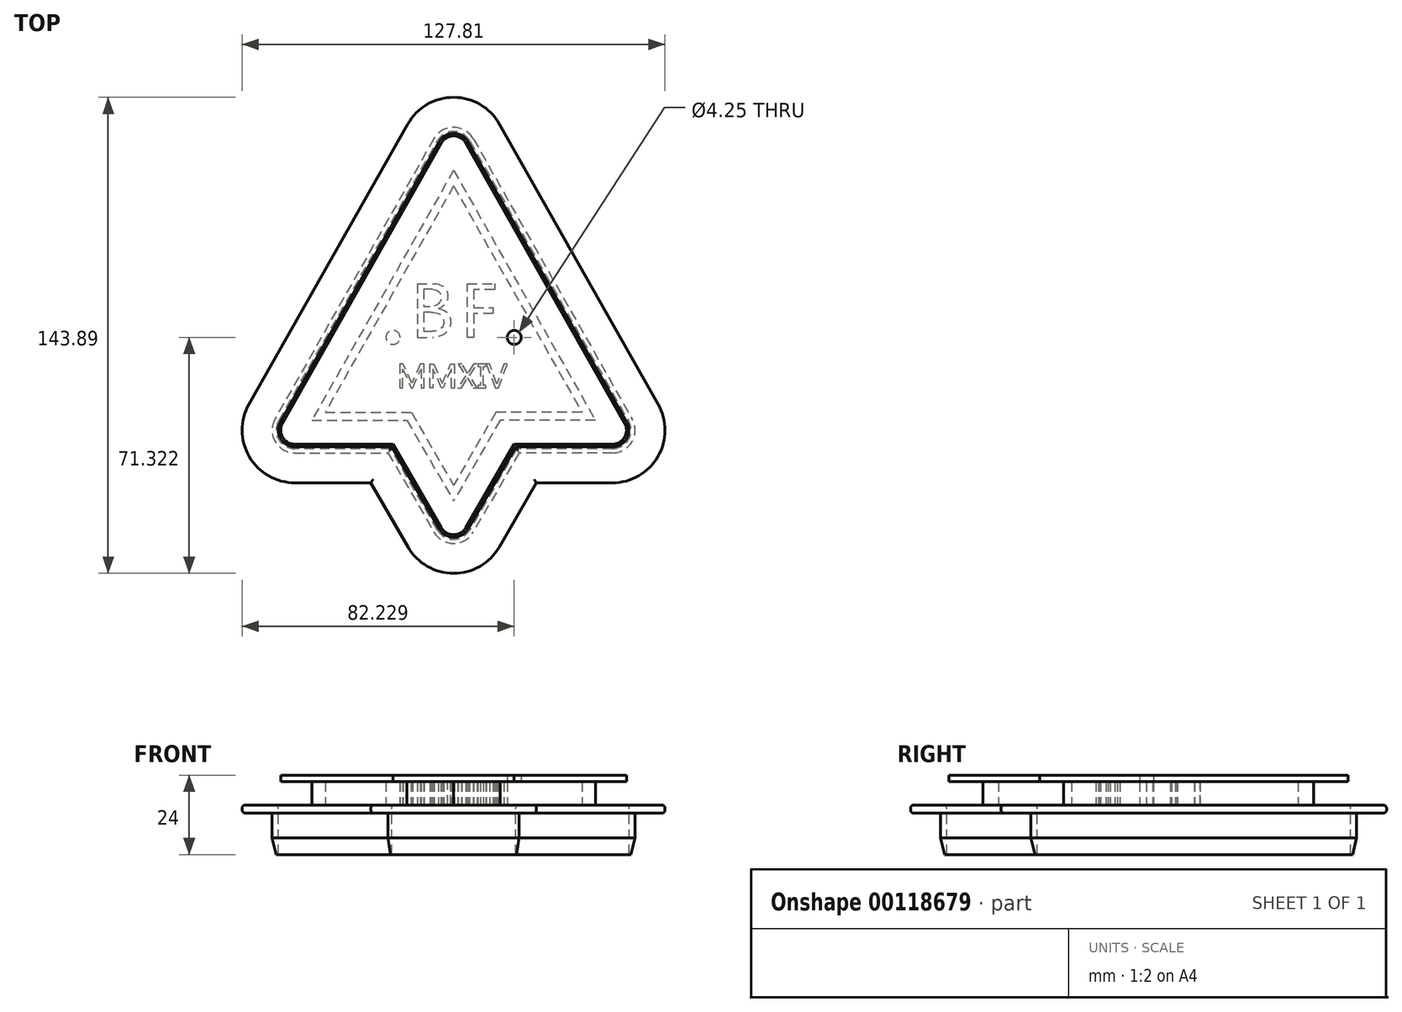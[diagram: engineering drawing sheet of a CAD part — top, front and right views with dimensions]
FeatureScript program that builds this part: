
annotation { "Feature Type Name" : "Feature", "Feature Type Description" : "" }
export const myFeature = defineFeature(function(context is Context, id is Id, definition is map)
    precondition{}
    {
        {
            var Q0;
            Q0=qCreatedBy(makeId("Top.planeOp"),FACE);
            var sketch = newSketch(context, id + "F0", { "sketchPlane" : qUnion([Q0])});
            skLineSegment(sketch, "E0", {"start": v(3.45, -76.83) * mm, "end": v(3.45, 23.17) * mm, "construction": true});
            skLineSegment(sketch, "E1", {"start": v(3.45, 23.17) * mm, "end": v(-39.41, -52.46) * mm});
            skLineSegment(sketch, "E2", {"start": v(-39.41, -52.46) * mm, "end": v(-10.65, -52.46) * mm});
            skLineSegment(sketch, "E3", {"start": v(-10.65, -52.46) * mm, "end": v(3.45, -76.83) * mm});
            skLineSegment(sketch, "E4.MirrorCS", {"start": v(17.54, -52.46) * mm, "end": v(3.45, -76.83) * mm});
            skLineSegment(sketch, "E5.MirrorCS", {"start": v(46.3, -52.46) * mm, "end": v(17.54, -52.46) * mm});
            skLineSegment(sketch, "E6.MirrorCS", {"start": v(3.45, 23.17) * mm, "end": v(46.3, -52.46) * mm});
            skLineSegment(sketch, "E7.0", {"start": v(7.8, 31.72) * mm, "end": v(55.8, -53) * mm});
            skLineSegment(sketch, "E7.1", {"start": v(-44.56, -60.46) * mm, "end": v(-15.26, -60.46) * mm});
            skLineSegment(sketch, "E7.2", {"start": v(-15.26, -60.46) * mm, "end": v(-0.88, -85.33) * mm});
            skLineSegment(sketch, "E7.3", {"start": v(-0.9, 31.72) * mm, "end": v(-48.9, -53) * mm});
            skLineSegment(sketch, "E7.4", {"start": v(22.16, -60.46) * mm, "end": v(7.77, -85.33) * mm});
            skLineSegment(sketch, "E7.5", {"start": v(51.45, -60.46) * mm, "end": v(22.16, -60.46) * mm});
            skLineSegment(sketch, "E8.0", {"start": v(3.45, 18.38) * mm, "end": v(42.25, -50.1) * mm});
            skLineSegment(sketch, "E8.1", {"start": v(-35.36, -50.1) * mm, "end": v(-9.29, -50.1) * mm});
            skLineSegment(sketch, "E8.2", {"start": v(-9.29, -50.1) * mm, "end": v(3.45, -72.12) * mm});
            skLineSegment(sketch, "E8.3", {"start": v(3.45, 18.38) * mm, "end": v(-35.36, -50.1) * mm});
            skLineSegment(sketch, "E8.4", {"start": v(16.18, -50.1) * mm, "end": v(3.45, -72.12) * mm});
            skLineSegment(sketch, "E8.5", {"start": v(42.25, -50.1) * mm, "end": v(16.18, -50.1) * mm});
            skPoint(sketch, "E9.visualSharp", {"position": v(3.45, 39.4) * mm});
            skArc(sketch, "E9.filletArc", {"start": v(7.8, 31.72) * mm, "mid": v(3.45, 34.25) * mm, "end": v(-0.9, 31.72) * mm});
            skPoint(sketch, "E10.visualSharp", {"position": v(-53.14, -60.46) * mm});
            skArc(sketch, "E10.filletArc", {"start": v(-48.9, -53) * mm, "mid": v(-48.88, -57.98) * mm, "end": v(-44.56, -60.46) * mm});
            skPoint(sketch, "E11.visualSharp", {"position": v(3.45, -92.81) * mm});
            skArc(sketch, "E11.filletArc", {"start": v(-0.88, -85.33) * mm, "mid": v(3.45, -87.82) * mm, "end": v(7.77, -85.33) * mm});
            skPoint(sketch, "E12.visualSharp", {"position": v(60.03, -60.46) * mm});
            skArc(sketch, "E12.filletArc", {"start": v(51.45, -60.46) * mm, "mid": v(55.77, -57.98) * mm, "end": v(55.8, -53) * mm});
            skLineSegment(sketch, "E13", {"start": v(-7.57, -11.13) * mm, "end": v(-7.57, -27.4) * mm});
            skLineSegment(sketch, "E14", {"start": v(-7.57, -27.4) * mm, "end": v(-2.15, -27.4) * mm});
            skLineSegment(sketch, "E15", {"start": v(-7.57, -11.13) * mm, "end": v(-2.43, -11.13) * mm});
            skLineSegment(sketch, "E16", {"start": v(-2.95, -12.9) * mm, "end": v(-5.58, -12.9) * mm});
            skLineSegment(sketch, "E17", {"start": v(-5.58, -12.9) * mm, "end": v(-5.58, -18.07) * mm});
            skLineSegment(sketch, "E18", {"start": v(-5.58, -18.07) * mm, "end": v(-3.65, -18.07) * mm});
            skLineSegment(sketch, "E19", {"start": v(-3.3, -19.84) * mm, "end": v(-5.58, -19.84) * mm});
            skLineSegment(sketch, "E20", {"start": v(-5.58, -19.84) * mm, "end": v(-5.58, -25.6) * mm});
            skLineSegment(sketch, "E21", {"start": v(-5.58, -25.6) * mm, "end": v(-2.88, -25.6) * mm});
            skFitSpline(sketch, "E22", {"points": [v(-2.95, -12.9) * mm, v(-1.55, -13.25) * mm, v(-0.77, -13.84) * mm, v(-0.4, -14.71) * mm, v(-0.38, -15.73) * mm, v(-0.61, -16.54) * mm, v(-1.06, -17.17) * mm, v(-1.75, -17.68) * mm, v(-2.43, -17.93) * mm, v(-3.27, -18.06) * mm, v(-3.65, -18.07) * mm], "startDerivative": vector(12.37, 0) * mm, "endDerivative": vector(-6.52, 0) * mm});
            skFitSpline(sketch, "E23", {"points": [v(-3.3, -19.84) * mm, v(-3.1, -19.84) * mm, v(-2.41, -19.88) * mm, v(-1.62, -20.03) * mm, v(-1.02, -20.26) * mm, v(-0.58, -20.52) * mm, v(-0.1, -20.94) * mm, v(0.27, -21.55) * mm, v(0.42, -22.11) * mm, v(0.46, -22.89) * mm, v(0.36, -23.57) * mm, v(0.05, -24.23) * mm, v(-0.37, -24.74) * mm, v(-0.99, -25.18) * mm, v(-1.82, -25.49) * mm, v(-2.55, -25.6) * mm, v(-2.88, -25.6) * mm], "startDerivative": vector(4.87, 0.06) * mm, "endDerivative": vector(-6.62, 0.23) * mm});
            skFitSpline(sketch, "E24", {"points": [v(-2.43, -11.13) * mm, v(-2.2, -11.13) * mm, v(-1.28, -11.3) * mm, v(-0.51, -11.57) * mm, v(0.21, -11.98) * mm, v(0.77, -12.45) * mm, v(1.21, -13.02) * mm, v(1.52, -13.67) * mm, v(1.66, -14.33) * mm, v(1.7, -15.05) * mm, v(1.6, -15.83) * mm, v(1.15, -16.97) * mm, v(0.59, -17.7) * mm, v(-0.29, -18.37) * mm, v(-1.14, -18.73) * mm], "startDerivative": vector(4.9, 0.32) * mm, "endDerivative": vector(-10.98, -3.88) * mm});
            skFitSpline(sketch, "E25", {"points": [v(-1.14, -18.73) * mm, v(-0.6, -18.81) * mm, v(0.06, -19) * mm, v(0.6, -19.25) * mm, v(1.07, -19.56) * mm, v(1.52, -19.96) * mm, v(1.92, -20.5) * mm, v(2.25, -21.13) * mm, v(2.45, -21.89) * mm, v(2.5, -22.84) * mm, v(2.41, -23.7) * mm, v(2.14, -24.56) * mm, v(1.71, -25.3) * mm, v(1.04, -26.04) * mm, v(0.2, -26.65) * mm, v(-0.94, -27.14) * mm, v(-2.04, -27.35) * mm, v(-2.81, -27.4) * mm], "startDerivative": vector(10.65, -1.4) * mm, "endDerivative": vector(-12.84, -0.61) * mm});
            skCircle(sketch, "E26", {"center": v(-14.88, -27.4) * mm, "radius": 2.13 * mm});
            skCircle(sketch, "E27.MirrorC", {"center": v(21.77, -27.4) * mm, "radius": 2.13 * mm});
            skLineSegment(sketch, "E28", {"start": v(7.57, -11.13) * mm, "end": v(15.83, -11.13) * mm});
            skLineSegment(sketch, "E29", {"start": v(15.83, -11.13) * mm, "end": v(15.83, -12.93) * mm});
            skLineSegment(sketch, "E30", {"start": v(15.83, -12.93) * mm, "end": v(9.53, -12.93) * mm});
            skLineSegment(sketch, "E31", {"start": v(9.53, -12.93) * mm, "end": v(9.53, -18.43) * mm});
            skLineSegment(sketch, "E32", {"start": v(9.53, -18.43) * mm, "end": v(15.38, -18.43) * mm});
            skLineSegment(sketch, "E33", {"start": v(15.38, -18.43) * mm, "end": v(15.38, -20.22) * mm});
            skLineSegment(sketch, "E34", {"start": v(15.38, -20.22) * mm, "end": v(9.53, -20.22) * mm});
            skLineSegment(sketch, "E35", {"start": v(9.53, -20.22) * mm, "end": v(9.53, -27.4) * mm});
            skLineSegment(sketch, "E36", {"start": v(9.53, -27.4) * mm, "end": v(7.57, -27.4) * mm});
            skLineSegment(sketch, "E37", {"start": v(7.57, -27.4) * mm, "end": v(7.57, -11.13) * mm});
            skLineSegment(sketch, "E38", {"start": v(-13.1, -42.69) * mm, "end": v(20.07, -42.69) * mm, "construction": true});
            skLineSegment(sketch, "E39", {"start": v(20.07, -42.69) * mm, "end": v(20.07, -35.42) * mm, "construction": true});
            skLineSegment(sketch, "E40", {"start": v(20.07, -35.42) * mm, "end": v(-13.1, -35.42) * mm, "construction": true});
            skLineSegment(sketch, "E41", {"start": v(-12.88, -35.42) * mm, "end": v(-12.88, -42.69) * mm});
            skLineSegment(sketch, "E42", {"start": v(-12.88, -42.69) * mm, "end": v(-11.95, -42.69) * mm});
            skLineSegment(sketch, "E43", {"start": v(-11.95, -42.69) * mm, "end": v(-11.95, -36.93) * mm});
            skLineSegment(sketch, "E44", {"start": v(-11.95, -36.93) * mm, "end": v(-9.4, -42.69) * mm});
            skLineSegment(sketch, "E45", {"start": v(-9.4, -42.69) * mm, "end": v(-8.95, -42.69) * mm});
            skLineSegment(sketch, "E46", {"start": v(-8.95, -42.69) * mm, "end": v(-6.4, -36.93) * mm});
            skLineSegment(sketch, "E47", {"start": v(-6.4, -36.93) * mm, "end": v(-6.4, -42.69) * mm});
            skLineSegment(sketch, "E48", {"start": v(-6.4, -42.69) * mm, "end": v(-5.46, -42.69) * mm});
            skLineSegment(sketch, "E49", {"start": v(-5.46, -42.69) * mm, "end": v(-5.46, -35.42) * mm});
            skLineSegment(sketch, "E50", {"start": v(-5.46, -35.42) * mm, "end": v(-6.6, -35.42) * mm});
            skLineSegment(sketch, "E51", {"start": v(-6.6, -35.42) * mm, "end": v(-9.18, -41.27) * mm});
            skLineSegment(sketch, "E52", {"start": v(-9.18, -41.27) * mm, "end": v(-11.77, -35.42) * mm});
            skLineSegment(sketch, "E53", {"start": v(-11.77, -35.42) * mm, "end": v(-12.88, -35.42) * mm});
            skLineSegment(sketch, "E54", {"start": v(-5.46, -42.69) * mm, "end": v(-3.71, -42.69) * mm});
            skLineSegment(sketch, "E55", {"start": v(-4.59, -42.69) * mm, "end": v(-4.59, -35.42) * mm, "construction": true});
            skLineSegment(sketch, "E56.MirrorCS", {"start": v(-3.71, -42.69) * mm, "end": v(-3.71, -35.42) * mm});
            skLineSegment(sketch, "E57.MirrorCS", {"start": v(-2.78, -36.93) * mm, "end": v(-2.78, -42.69) * mm});
            skLineSegment(sketch, "E58.MirrorCS", {"start": v(-0.23, -42.69) * mm, "end": v(-2.78, -36.93) * mm});
            skLineSegment(sketch, "E59.MirrorCS", {"start": v(-2.59, -35.42) * mm, "end": v(0, -41.27) * mm});
            skLineSegment(sketch, "E60.MirrorCS", {"start": v(-29.24, -35.42) * mm, "end": v(3.91, -35.42) * mm, "construction": true});
            skLineSegment(sketch, "E61.MirrorCS", {"start": v(0, -41.27) * mm, "end": v(2.59, -35.42) * mm});
            skLineSegment(sketch, "E62.MirrorCS", {"start": v(2.77, -36.93) * mm, "end": v(0.23, -42.69) * mm});
            skLineSegment(sketch, "E63.MirrorCS", {"start": v(2.77, -42.69) * mm, "end": v(2.77, -36.93) * mm});
            skLineSegment(sketch, "E64.MirrorCS", {"start": v(3.7, -35.42) * mm, "end": v(3.7, -42.69) * mm});
            skLineSegment(sketch, "E65", {"start": v(-3.71, -35.42) * mm, "end": v(-2.59, -35.42) * mm});
            skLineSegment(sketch, "E66", {"start": v(2.59, -35.42) * mm, "end": v(3.7, -35.42) * mm});
            skLineSegment(sketch, "E67", {"start": v(2.77, -42.69) * mm, "end": v(3.7, -42.69) * mm});
            skLineSegment(sketch, "E68", {"start": v(0.23, -42.69) * mm, "end": v(-0.23, -42.69) * mm});
            skLineSegment(sketch, "E69", {"start": v(-2.78, -42.69) * mm, "end": v(-3.71, -42.69) * mm});
            skLineSegment(sketch, "E70", {"start": v(4.83, -35.42) * mm, "end": v(7.09, -39.05) * mm});
            skLineSegment(sketch, "E71", {"start": v(7.09, -39.05) * mm, "end": v(4.64, -42.69) * mm});
            skLineSegment(sketch, "E72", {"start": v(4.64, -42.69) * mm, "end": v(5.8, -42.69) * mm});
            skLineSegment(sketch, "E73", {"start": v(5.8, -42.69) * mm, "end": v(7.63, -39.64) * mm});
            skLineSegment(sketch, "E74", {"start": v(7.63, -39.64) * mm, "end": v(9.44, -42.69) * mm});
            skLineSegment(sketch, "E75", {"start": v(9.44, -42.69) * mm, "end": v(10.56, -42.69) * mm});
            skLineSegment(sketch, "E76", {"start": v(10.56, -42.69) * mm, "end": v(8.26, -39.05) * mm});
            skLineSegment(sketch, "E77", {"start": v(8.26, -39.05) * mm, "end": v(10.54, -35.42) * mm});
            skLineSegment(sketch, "E78", {"start": v(10.54, -35.42) * mm, "end": v(9.48, -35.42) * mm});
            skLineSegment(sketch, "E79", {"start": v(9.48, -35.42) * mm, "end": v(7.67, -38.4) * mm});
            skLineSegment(sketch, "E80", {"start": v(7.67, -38.4) * mm, "end": v(5.94, -35.42) * mm});
            skLineSegment(sketch, "E81", {"start": v(5.94, -35.42) * mm, "end": v(4.83, -35.42) * mm});
            skLineSegment(sketch, "E82", {"start": v(10.82, -35.42) * mm, "end": v(10.82, -36.25) * mm});
            skLineSegment(sketch, "E83", {"start": v(10.82, -36.25) * mm, "end": v(11.5, -36.25) * mm});
            skLineSegment(sketch, "E84", {"start": v(11.5, -36.25) * mm, "end": v(11.5, -41.9) * mm});
            skLineSegment(sketch, "E85", {"start": v(11.5, -41.9) * mm, "end": v(10.82, -41.9) * mm});
            skLineSegment(sketch, "E86", {"start": v(10.82, -41.9) * mm, "end": v(10.82, -42.69) * mm});
            skLineSegment(sketch, "E87", {"start": v(10.82, -42.69) * mm, "end": v(13.16, -42.69) * mm});
            skLineSegment(sketch, "E88", {"start": v(13.16, -42.69) * mm, "end": v(13.16, -41.9) * mm});
            skLineSegment(sketch, "E89", {"start": v(13.16, -41.9) * mm, "end": v(12.43, -41.9) * mm});
            skLineSegment(sketch, "E90", {"start": v(12.43, -41.9) * mm, "end": v(12.43, -36.25) * mm});
            skLineSegment(sketch, "E91", {"start": v(12.43, -36.25) * mm, "end": v(13.15, -36.25) * mm});
            skPoint(sketch, "E91.endSnap0", {"position": v(11.16, -36.25) * mm});
            skLineSegment(sketch, "E92", {"start": v(13.15, -36.25) * mm, "end": v(13.15, -35.42) * mm});
            skLineSegment(sketch, "E93", {"start": v(13.15, -35.42) * mm, "end": v(10.82, -35.42) * mm});
            skLineSegment(sketch, "E94", {"start": v(13.37, -35.42) * mm, "end": v(16.02, -42.69) * mm});
            skLineSegment(sketch, "E95", {"start": v(16.02, -42.69) * mm, "end": v(16.98, -42.69) * mm});
            skLineSegment(sketch, "E96", {"start": v(16.98, -42.69) * mm, "end": v(19.67, -35.42) * mm});
            skLineSegment(sketch, "E97", {"start": v(19.67, -35.42) * mm, "end": v(18.67, -35.42) * mm});
            skLineSegment(sketch, "E98", {"start": v(18.67, -35.42) * mm, "end": v(16.5, -41.54) * mm});
            skLineSegment(sketch, "E99", {"start": v(16.5, -41.54) * mm, "end": v(14.4, -35.42) * mm});
            skLineSegment(sketch, "E100", {"start": v(14.4, -35.42) * mm, "end": v(13.37, -35.42) * mm});
            skArc(sketch, "E101.0", {"start": v(9.4, 32.63) * mm, "mid": v(3.45, 36.1) * mm, "end": v(-2.51, 32.63) * mm});
            skLineSegment(sketch, "E101.1", {"start": v(9.4, 32.63) * mm, "end": v(57.4, -52.08) * mm});
            skLineSegment(sketch, "E101.2", {"start": v(-2.51, 32.63) * mm, "end": v(-50.52, -52.08) * mm});
            skArc(sketch, "E101.3", {"start": v(51.45, -62.31) * mm, "mid": v(57.37, -58.91) * mm, "end": v(57.4, -52.08) * mm});
            skLineSegment(sketch, "E101.4", {"start": v(51.45, -62.31) * mm, "end": v(23.22, -62.31) * mm});
            skLineSegment(sketch, "E101.5", {"start": v(23.22, -62.31) * mm, "end": v(9.38, -86.25) * mm});
            skArc(sketch, "E101.6", {"start": v(-50.52, -52.08) * mm, "mid": v(-50.48, -58.91) * mm, "end": v(-44.56, -62.31) * mm});
            skLineSegment(sketch, "E101.7", {"start": v(-44.56, -62.31) * mm, "end": v(-16.33, -62.31) * mm});
            skLineSegment(sketch, "E101.8", {"start": v(-16.33, -62.31) * mm, "end": v(-2.48, -86.25) * mm});
            skArc(sketch, "E101.9", {"start": v(-2.48, -86.25) * mm, "mid": v(3.45, -89.67) * mm, "end": v(9.38, -86.25) * mm});
            skLineSegment(sketch, "E102.0", {"start": v(17.28, 37.1) * mm, "end": v(65.29, -47.62) * mm});
            skArc(sketch, "E102.1", {"start": v(51.45, -71.37) * mm, "mid": v(65.2, -63.47) * mm, "end": v(65.29, -47.62) * mm});
            skArc(sketch, "E102.2", {"start": v(17.28, 37.1) * mm, "mid": v(3.45, 45.16) * mm, "end": v(-10.4, 37.1) * mm});
            skLineSegment(sketch, "E102.3", {"start": v(51.45, -71.37) * mm, "end": v(28.45, -71.37) * mm});
            skLineSegment(sketch, "E102.4", {"start": v(28.45, -71.37) * mm, "end": v(17.21, -90.79) * mm});
            skArc(sketch, "E102.5", {"start": v(-10.32, -90.79) * mm, "mid": v(3.45, -98.73) * mm, "end": v(17.21, -90.79) * mm});
            skLineSegment(sketch, "E102.6", {"start": v(-10.4, 37.1) * mm, "end": v(-58.4, -47.62) * mm});
            skArc(sketch, "E102.7", {"start": v(-58.4, -47.62) * mm, "mid": v(-58.3, -63.47) * mm, "end": v(-44.56, -71.37) * mm});
            skLineSegment(sketch, "E102.8", {"start": v(-44.56, -71.37) * mm, "end": v(-21.56, -71.37) * mm});
            skLineSegment(sketch, "E102.9", {"start": v(-21.56, -71.37) * mm, "end": v(-10.32, -90.79) * mm});
            skSolve(sketch);
        }
        {
            var Q0;
            Q0=makeQuery(id+"F0.imprint","IMPRINT",FACE,{"disambiguationData":[TD([[makeQuery(id+"F0.imprint","IMPRINT",EDGE,{"derivedFrom":sQuery(id+"F0.wireOp",EDGE,"E101.0")}),-1.0]])]});
            extrude(context, id + "F1", {"entities" : qUnion([Q0]), "oppositeDirection" : true, "depth" : 2.5 * mm});
        }
        {
            var Q0;
            Q0=makeQuery(id+"F0.imprint","IMPRINT",FACE,{"disambiguationData":[TD([[makeQuery(id+"F0.imprint","IMPRINT",EDGE,{"derivedFrom":sQuery(id+"F0.wireOp",EDGE,"E7.0")}),1.0]])]});
            extrude(context, id + "F2", {"entities" : qUnion([Q0]), "operationType" : NewBodyOperationType.ADD, "oppositeDirection" : true, "depth" : 15 * mm});
        }
        {
            var Q0;
            Q0=makeQuery(id+"F0.imprint","IMPRINT",FACE,{"disambiguationData":[TD([[makeQuery(id+"F0.imprint","IMPRINT",EDGE,{"derivedFrom":sQuery(id+"F0.wireOp",EDGE,"E1")}),-1.0]])]});
            var Q1;
            Q1=makeQuery(id+"F0.imprint","IMPRINT",FACE,{"disambiguationData":[TD([[makeQuery(id+"F0.imprint","IMPRINT",EDGE,{"derivedFrom":sQuery(id+"F0.wireOp",EDGE,"E1")}),1.0]])]});
            var Q2;
            Q2=makeQuery(id+"F0.imprint","IMPRINT",FACE,{"disambiguationData":[TD([[makeQuery(id+"F0.imprint","IMPRINT",EDGE,{"derivedFrom":sQuery(id+"F0.wireOp",EDGE,"E8.0")}),-1.0]])]});
            var Q3;
            {var subQ1=sQuery(id+"F0.wireOp",EDGE,"E13");Q3=makeQuery(id+"F0.imprint","IMPRINT",FACE,{"disambiguationData":[TD([[makeQuery(id+"F0.imprint","IMPRINT",EDGE,{"derivedFrom":subQ1}),1.0]])]});}
            var Q4;
            Q4=makeQuery(id+"F0.imprint","IMPRINT",FACE,{"disambiguationData":[TD([[makeQuery(id+"F0.imprint","IMPRINT",EDGE,{"derivedFrom":sQuery(id+"F0.wireOp",EDGE,"E16")}),1.0]])]});
            var Q5;
            Q5=makeQuery(id+"F0.imprint","IMPRINT",FACE,{"disambiguationData":[TD([[makeQuery(id+"F0.imprint","IMPRINT",EDGE,{"derivedFrom":sQuery(id+"F0.wireOp",EDGE,"E19")}),1.0]])]});
            var Q6;
            Q6=makeQuery(id+"F0.imprint","IMPRINT",FACE,{"disambiguationData":[TD([[makeQuery(id+"F0.imprint","IMPRINT",EDGE,{"derivedFrom":sQuery(id+"F0.wireOp",EDGE,"E28")}),-1.0]])]});
            var Q7;
            Q7=makeQuery(id+"F0.imprint","IMPRINT",FACE,{"disambiguationData":[TD([[makeQuery(id+"F0.imprint","IMPRINT",EDGE,{"derivedFrom":sQuery(id+"F0.wireOp",EDGE,"E27.MirrorC")}),-1.0]])]});
            var Q8;
            Q8=makeQuery(id+"F0.imprint","IMPRINT",FACE,{"disambiguationData":[TD([[makeQuery(id+"F0.imprint","IMPRINT",EDGE,{"derivedFrom":sQuery(id+"F0.wireOp",EDGE,"E94")}),1.0]])]});
            var Q9;
            Q9=makeQuery(id+"F0.imprint","IMPRINT",FACE,{"disambiguationData":[TD([[makeQuery(id+"F0.imprint","IMPRINT",EDGE,{"derivedFrom":sQuery(id+"F0.wireOp",EDGE,"E82")}),1.0]])]});
            var Q10;
            Q10=makeQuery(id+"F0.imprint","IMPRINT",FACE,{"disambiguationData":[TD([[makeQuery(id+"F0.imprint","IMPRINT",EDGE,{"derivedFrom":sQuery(id+"F0.wireOp",EDGE,"E70")}),1.0]])]});
            var Q11;
            Q11=makeQuery(id+"F0.imprint","IMPRINT",FACE,{"disambiguationData":[TD([[makeQuery(id+"F0.imprint","IMPRINT",EDGE,{"derivedFrom":sQuery(id+"F0.wireOp",EDGE,"E56.MirrorCS")}),-1.0]])]});
            var Q12;
            Q12=makeQuery(id+"F0.imprint","IMPRINT",FACE,{"disambiguationData":[TD([[makeQuery(id+"F0.imprint","IMPRINT",EDGE,{"derivedFrom":sQuery(id+"F0.wireOp",EDGE,"E41")}),1.0]])]});
            var Q13;
            Q13=makeQuery(id+"F0.imprint","IMPRINT",FACE,{"disambiguationData":[TD([[makeQuery(id+"F0.imprint","IMPRINT",EDGE,{"derivedFrom":sQuery(id+"F0.wireOp",EDGE,"E26")}),1.0]])]});
            extrude(context, id + "F3", {"entities" : qUnion([Q0, Q1, Q2, Q3, Q4, Q5, Q6, Q7, Q8, Q9, Q10, Q11, Q12, Q13]), "depth" : 15 * mm});
        }
        {
            var Q0;
            Q0=makeQuery(id+"F0.imprint","IMPRINT",FACE,{"disambiguationData":[TD([[makeQuery(id+"F0.imprint","IMPRINT",EDGE,{"derivedFrom":sQuery(id+"F0.wireOp",EDGE,"E8.0")}),-1.0]])]});
            var Q1;
            Q1=makeQuery(id+"F0.imprint","IMPRINT",FACE,{"disambiguationData":[TD([[makeQuery(id+"F0.imprint","IMPRINT",EDGE,{"derivedFrom":sQuery(id+"F0.wireOp",EDGE,"E1")}),-1.0]])]});
            var Q2;
            Q2=makeQuery(id+"F0.imprint","IMPRINT",FACE,{"disambiguationData":[TD([[makeQuery(id+"F0.imprint","IMPRINT",EDGE,{"derivedFrom":sQuery(id+"F0.wireOp",EDGE,"E16")}),1.0]])]});
            var Q3;
            Q3=makeQuery(id+"F0.imprint","IMPRINT",FACE,{"disambiguationData":[TD([[makeQuery(id+"F0.imprint","IMPRINT",EDGE,{"derivedFrom":sQuery(id+"F0.wireOp",EDGE,"E19")}),1.0]])]});
            extrude(context, id + "F4", {"entities" : qUnion([Q0, Q1, Q2, Q3]), "operationType" : NewBodyOperationType.REMOVE, "depth" : 7 * mm});
        }
        {
            var Q0;
            Q0=makeQuery(id+"F2.opExtrude","CAP_EDGE",EDGE,{"disambiguationData":[OSD([sQuery(id+"F0.wireOp",EDGE,"E101.2")])],"isStart":false});
            var Q1;
            Q1=makeQuery(id+"F2.opExtrude","CAP_EDGE",EDGE,{"disambiguationData":[OSD([sQuery(id+"F0.wireOp",EDGE,"E101.6")])],"isStart":false});
            var Q2;
            Q2=makeQuery(id+"F2.opExtrude","CAP_EDGE",EDGE,{"disambiguationData":[OSD([sQuery(id+"F0.wireOp",EDGE,"E101.7")])],"isStart":false});
            var Q3;
            Q3=makeQuery(id+"F2.opExtrude","CAP_EDGE",EDGE,{"disambiguationData":[OSD([sQuery(id+"F0.wireOp",EDGE,"E101.8")])],"isStart":false});
            chamfer(context, id + "F5", {"entities" : qUnion([Q0, Q1, Q2, Q3]), "chamferType" : ChamferType.TWO_OFFSETS, "width1" : 5 * mm, "oppositeDirection" : false, "width2" : 1.25 * mm, "tangentPropagation" : true});
        }
        {
            var Q0;
            Q0=makeQuery(id+"F1.opExtrude","CAP_EDGE",EDGE,{"disambiguationData":[OSD([sQuery(id+"F0.wireOp",EDGE,"E101.2")])],"isStart":false});
            var Q1;
            Q1=makeQuery(id+"F1.opExtrude","CAP_EDGE",EDGE,{"disambiguationData":[OSD([sQuery(id+"F0.wireOp",EDGE,"E102.6")])],"isStart":false});
            var Q2;
            Q2=makeQuery(id+"F1.opExtrude","CAP_EDGE",EDGE,{"disambiguationData":[OSD([sQuery(id+"F0.wireOp",EDGE,"E102.6")])],"isStart":true});
            var Q3;
            Q3=makeQuery(id+"F1.opExtrude","CAP_EDGE",EDGE,{"disambiguationData":[OSD([sQuery(id+"F0.wireOp",EDGE,"E102.9")])],"isStart":false});
            var Q4;
            Q4=makeQuery(id+"F1.opExtrude","CAP_EDGE",EDGE,{"disambiguationData":[OSD([sQuery(id+"F0.wireOp",EDGE,"E102.9")])],"isStart":true});
            var Q5;
            Q5=makeQuery(id+"F2.opExtrude","CAP_EDGE",EDGE,{"disambiguationData":[OSD([sQuery(id+"F0.wireOp",EDGE,"E7.0")])],"isStart":true});
            var Q6;
            Q6=makeQuery(id+"F2.opExtrude","CAP_EDGE",EDGE,{"disambiguationData":[OSD([sQuery(id+"F0.wireOp",EDGE,"E7.2")])],"isStart":true});
            var Q7;
            Q7=makeQuery(id+"F1.opExtrude","CAP_EDGE",EDGE,{"disambiguationData":[OSD([sQuery(id+"F0.wireOp",EDGE,"E101.5")])],"isStart":false});
            fillet(context, id + "F6", {"entities" : qUnion([Q0, Q1, Q2, Q3, Q4, Q5, Q6, Q7]), "radius" : 1 * mm, "tangentPropagation" : true, "allowEdgeOverflow" : false});
        }
        {
            var Q0;
            Q0=makeQuery(id+"F3.opExtrude","CAP_FACE",FACE,{"disambiguationData":[OSD([sQuery(id+"F0.wireOp",EDGE,"E7.0"),sQuery(id+"F0.wireOp",EDGE,"E7.1"),sQuery(id+"F0.wireOp",EDGE,"E7.2"),sQuery(id+"F0.wireOp",EDGE,"E7.3"),sQuery(id+"F0.wireOp",EDGE,"E7.4"),sQuery(id+"F0.wireOp",EDGE,"E7.5"),sQuery(id+"F0.wireOp",EDGE,"E9.filletArc"),sQuery(id+"F0.wireOp",EDGE,"E10.filletArc"),sQuery(id+"F0.wireOp",EDGE,"E11.filletArc"),sQuery(id+"F0.wireOp",EDGE,"E12.filletArc")])],"isStart":false});
            var sketch = newSketch(context, id + "F7", { "sketchPlane" : qUnion([Q0])});
            skArc(sketch, "E103.0", {"start": v(7.14, 31.35) * mm, "mid": v(3.45, 33.5) * mm, "end": v(-0.25, 31.35) * mm});
            skLineSegment(sketch, "E103.1", {"start": v(-0.25, 31.35) * mm, "end": v(-48.26, -53.37) * mm});
            skLineSegment(sketch, "E103.2", {"start": v(7.14, 31.35) * mm, "end": v(55.15, -53.37) * mm});
            skArc(sketch, "E103.3", {"start": v(-48.26, -53.37) * mm, "mid": v(-48.23, -57.6) * mm, "end": v(-44.56, -59.71) * mm});
            skLineSegment(sketch, "E103.4", {"start": v(-44.56, -59.71) * mm, "end": v(-14.83, -59.71) * mm});
            skLineSegment(sketch, "E103.5", {"start": v(-14.83, -59.71) * mm, "end": v(-0.23, -84.95) * mm});
            skArc(sketch, "E103.6", {"start": v(51.45, -59.71) * mm, "mid": v(55.12, -57.6) * mm, "end": v(55.15, -53.37) * mm});
            skLineSegment(sketch, "E103.7", {"start": v(51.45, -59.71) * mm, "end": v(21.72, -59.71) * mm});
            skLineSegment(sketch, "E103.8", {"start": v(21.72, -59.71) * mm, "end": v(7.12, -84.95) * mm});
            skArc(sketch, "E103.9", {"start": v(-0.23, -84.95) * mm, "mid": v(3.45, -87.07) * mm, "end": v(7.12, -84.95) * mm});
            skSolve(sketch);
        }
        {
            var Q0;
            Q0=makeQuery(id+"F7.imprint","IMPRINT",FACE,{"disambiguationData":[TD([[makeQuery(id+"F7.imprint","IMPRINT",EDGE,{"derivedFrom":sQuery(id+"F7.wireOp",EDGE,"E103.0")}),-1.0]])]});
            extrude(context, id + "F8", {"entities" : qUnion([Q0]), "operationType" : NewBodyOperationType.REMOVE, "oppositeDirection" : true, "depth" : 25 * mm});
        }
        {
            var Q0;
            Q0=makeQuery(id+"F3.opExtrude","CAP_FACE",FACE,{"disambiguationData":[OSD([sQuery(id+"F0.wireOp",EDGE,"E7.0"),sQuery(id+"F0.wireOp",EDGE,"E7.1"),sQuery(id+"F0.wireOp",EDGE,"E7.2"),sQuery(id+"F0.wireOp",EDGE,"E7.3"),sQuery(id+"F0.wireOp",EDGE,"E7.4"),sQuery(id+"F0.wireOp",EDGE,"E7.5"),sQuery(id+"F0.wireOp",EDGE,"E9.filletArc"),sQuery(id+"F0.wireOp",EDGE,"E10.filletArc"),sQuery(id+"F0.wireOp",EDGE,"E11.filletArc"),sQuery(id+"F0.wireOp",EDGE,"E12.filletArc")])],"isStart":false});
            extrude(context, id + "F9", {"entities" : qUnion([Q0]), "operationType" : NewBodyOperationType.REMOVE, "oppositeDirection" : true, "depth" : 6 * mm});
        }
    });
